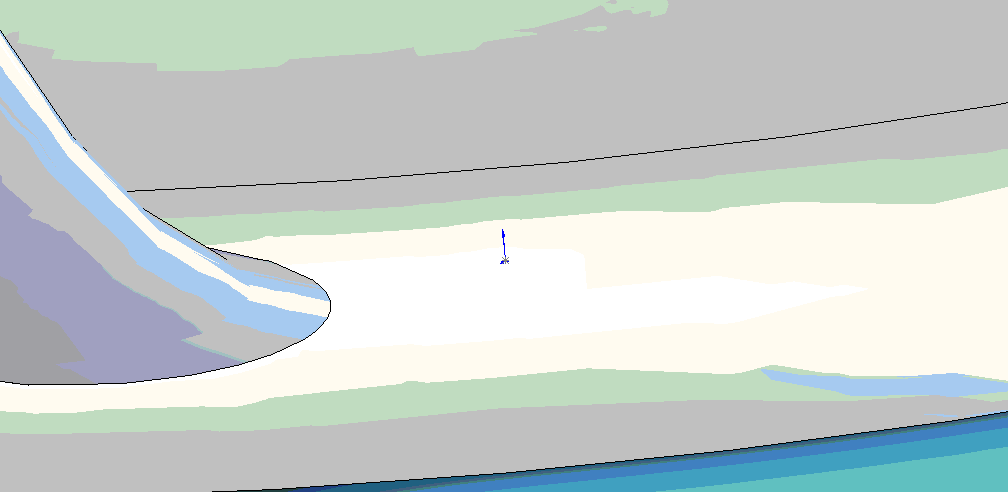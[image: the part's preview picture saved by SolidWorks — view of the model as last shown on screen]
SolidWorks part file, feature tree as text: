
SOLIDWORKS PART (.sldprt)
format: sldprt  version: not decoded by parser v0  size: 232,960 bytes
history: native  units: mm
features: sketch x4, plane x3, material x1, revolve x1, sweep x1, dome x1, cut_extrude x1 (+12 scaffold rows collapsed)
feature tree (24):
  scaffold x12  (default folders/planes/origin — collapsed)
  material  "PP Copolymer"
  plane  "Alzado"
  plane  "Planta"
  plane  "Vista lateral"
  sketch  "Croquis1"  dims[c1.D4=10.0mm c1.D5=20.0mm c1.D7=60.0mm c1.D8=12.5mm c1.D9=12.5mm c2.D7=60.0mm c2.D8=12.5mm c2.D9=12.5mm c3.D8=60.0mm c3.D7=60.0mm c4.D8=12.5mm c4.D7=60.0mm c4.D10=20.0mm c4.D5=20.0mm c5.D10=12.5mm c5.D7=60.0mm c5.D8=12.5mm c5.D1=220.0mm c5.D2=20.0mm c5.D3=90.0mm c5.D6=40.0mm c6.D7=40.0mm c6.D9=20.0mm c6.D10=20.0mm]
  revolve  "Revolución1"  Angle=360deg
  sketch  "Croquis2"  dims[D2=150.0mm D3=20.0mm D1=60.0mm D4=65.0mm D5=10.0mm]
  sketch  "Croquis4"  dims[D1=35.0mm D2=10.0mm]
  sweep  "Barrer1"
  dome  "Cúpula1"
  sketch  "Croquis5"  dims[D1=30.0mm]
  cut_extrude  "Cortar-Extruir1"  Depth=25mm
decode coverage: 6 of 8 modeling features carry decoded parameters
note: suppression state not decoded; provenance and decode notes live in map.json
